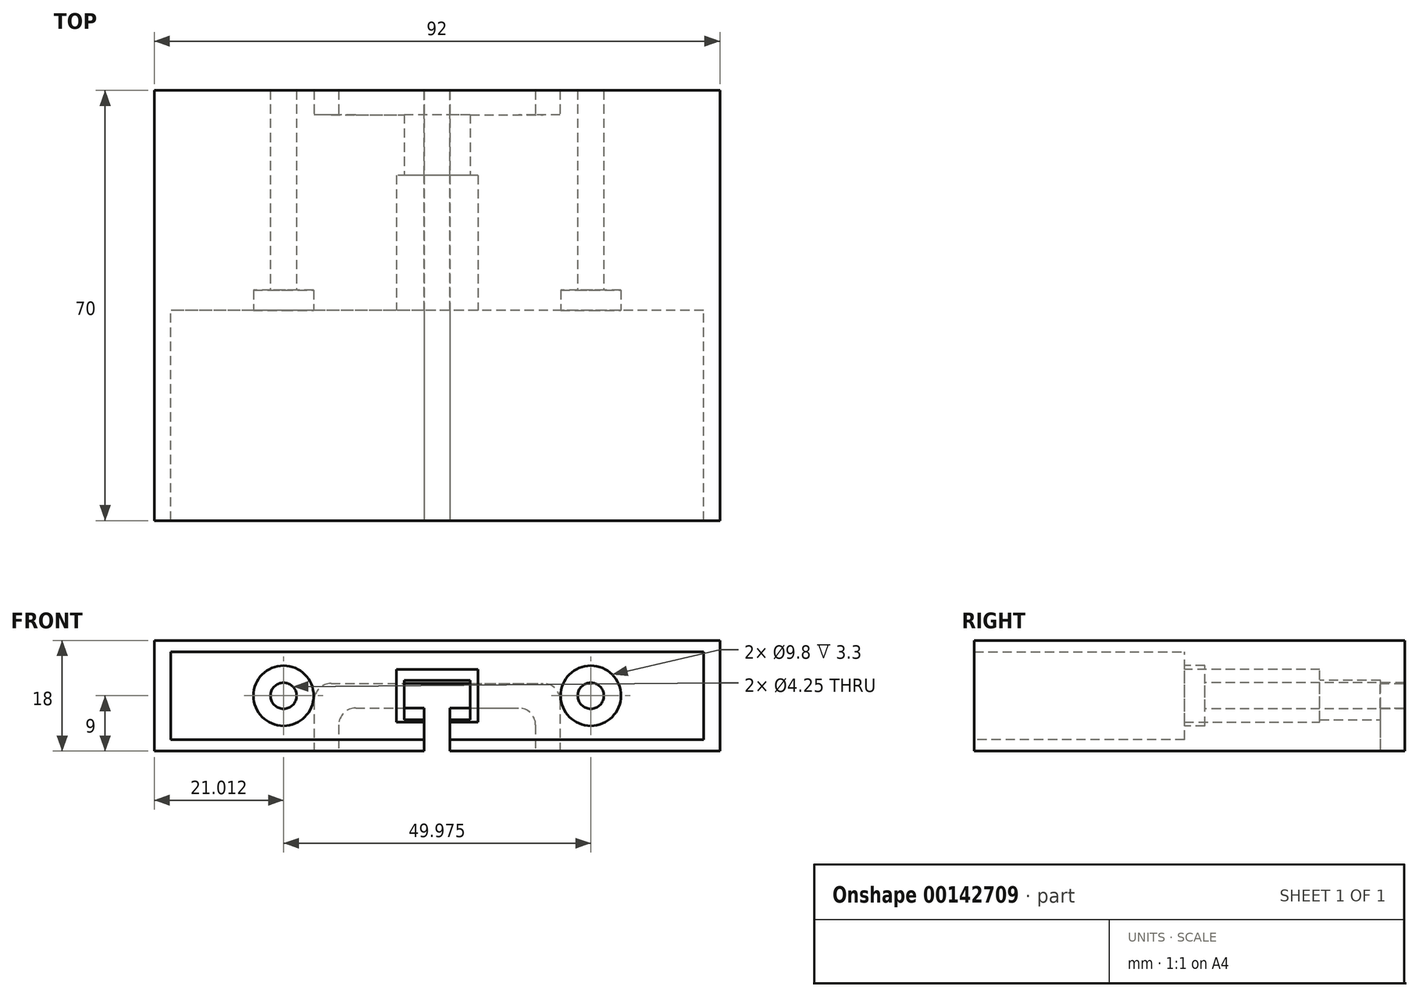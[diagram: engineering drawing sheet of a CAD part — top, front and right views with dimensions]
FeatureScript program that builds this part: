
annotation { "Feature Type Name" : "Feature", "Feature Type Description" : "" }
export const myFeature = defineFeature(function(context is Context, id is Id, definition is map)
    precondition{}
    {
        {
            var Q0;
            Q0=qCreatedBy(makeId("Front.planeOp"),FACE);
            var sketch = newSketch(context, id + "F0", { "sketchPlane" : qUnion([Q0])});
            skLineSegment(sketch, "E0.bottom", {"start": v(46, -9) * mm, "end": v(-46, -9) * mm});
            skLineSegment(sketch, "E0.top", {"start": v(46, 9) * mm, "end": v(-46, 9) * mm});
            skLineSegment(sketch, "E0.left", {"start": v(46, -9) * mm, "end": v(46, 9) * mm});
            skLineSegment(sketch, "E0.right", {"start": v(-46, -9) * mm, "end": v(-46, 9) * mm});
            skPoint(sketch, "E0.middle", {"position": v(0, 0) * mm});
            skLineSegment(sketch, "E1.bottom", {"start": v(43.33, -7.12) * mm, "end": v(-43.33, -7.13) * mm});
            skLineSegment(sketch, "E1.top", {"start": v(43.33, 7.13) * mm, "end": v(-43.33, 7.12) * mm});
            skLineSegment(sketch, "E1.left", {"start": v(43.33, -7.12) * mm, "end": v(43.33, 7.13) * mm});
            skLineSegment(sketch, "E1.right", {"start": v(-43.33, -7.13) * mm, "end": v(-43.33, 7.12) * mm});
            skSolve(sketch);
        }
        {
            var Q0;
            Q0=makeQuery(id+"F0.imprint","IMPRINT",FACE,{"disambiguationData":[TD([[makeQuery(id+"F0.imprint","IMPRINT",EDGE,{"derivedFrom":sQuery(id+"F0.wireOp",EDGE,"E0.bottom")}),-1.0]])]});
            extrude(context, id + "F1", {"entities" : qUnion([Q0]), "depth" : 70 * mm, "offsetDistance" : 25 * mm});
        }
        {
            var Q0;
            Q0=makeQuery(id+"F0.imprint","IMPRINT",FACE,{"disambiguationData":[TD([[makeQuery(id+"F0.imprint","IMPRINT",EDGE,{"derivedFrom":sQuery(id+"F0.wireOp",EDGE,"E1.bottom")}),-1.0]])]});
            extrude(context, id + "F2", {"entities" : qUnion([Q0]), "operationType" : NewBodyOperationType.ADD, "depth" : 35.8 * mm, "offsetDistance" : 25 * mm});
        }
        {
            var Q0;
            Q0=qCreatedBy(makeId("Front.planeOp"),FACE);
            var sketch = newSketch(context, id + "F3", { "sketchPlane" : qUnion([Q0])});
            skPoint(sketch, "E2.middle", {"position": v(0, 0) * mm});
            skCircle(sketch, "E3", {"center": v(0, 0) * mm, "radius": 2 * mm});
            skSolve(sketch);
        }
        {
            var Q0;
            Q0=makeQuery(id+"F2.opExtrude","CAP_FACE",FACE,{"disambiguationData":[OSD([sQuery(id+"F0.wireOp",EDGE,"E1.bottom"),sQuery(id+"F0.wireOp",EDGE,"E1.top"),sQuery(id+"F0.wireOp",EDGE,"E1.left"),sQuery(id+"F0.wireOp",EDGE,"E1.right")])],"isStart":false});
            var sketch = newSketch(context, id + "F4", { "sketchPlane" : qUnion([Q0])});
            skLineSegment(sketch, "E4.bottom", {"start": v(6.65, -4.3) * mm, "end": v(-6.65, -4.3) * mm});
            skLineSegment(sketch, "E4.top", {"start": v(6.65, 4.3) * mm, "end": v(-6.65, 4.3) * mm});
            skLineSegment(sketch, "E4.left", {"start": v(6.65, -4.3) * mm, "end": v(6.65, 4.3) * mm});
            skLineSegment(sketch, "E4.right", {"start": v(-6.65, -4.3) * mm, "end": v(-6.65, 4.3) * mm});
            skPoint(sketch, "E4.middle", {"position": v(0, 0) * mm});
            skSolve(sketch);
        }
        {
            var Q0;
            Q0=makeQuery(id+"F4.imprint","IMPRINT",FACE,{"disambiguationData":[TD([[makeQuery(id+"F4.imprint","IMPRINT",EDGE,{"derivedFrom":sQuery(id+"F4.wireOp",EDGE,"E4.bottom")}),-1.0]])]});
            extrude(context, id + "F5", {"entities" : qUnion([Q0]), "operationType" : NewBodyOperationType.REMOVE, "oppositeDirection" : true, "depth" : 22 * mm, "offsetDistance" : 25 * mm});
        }
        {
            var Q0;
            Q0 = qSketchRegion(id + "F3", true);
            extrude(context, id + "F6", {"entities" : qUnion([Q0]), "operationType" : NewBodyOperationType.REMOVE, "depth" : 8 * mm, "offsetDistance" : 25 * mm});
        }
        {
            var Q0;
            Q0=qCreatedBy(makeId("Front.planeOp"),FACE);
            var sketch = newSketch(context, id + "F7", { "sketchPlane" : qUnion([Q0])});
            skLineSegment(sketch, "E5.bottom", {"start": v(-13.25, -2) * mm, "end": v(13.25, -2) * mm});
            skLineSegment(sketch, "E5.top", {"start": v(-17.25, 2) * mm, "end": v(17.25, 2) * mm});
            skLineSegment(sketch, "E5.left", {"start": v(-20, -2) * mm, "end": v(-20, -0.75) * mm});
            skLineSegment(sketch, "E5.right", {"start": v(20, -2) * mm, "end": v(20, -0.75) * mm});
            skPoint(sketch, "E5.middle", {"position": v(0, 0) * mm});
            skLineSegment(sketch, "E6.bottom", {"start": v(17.25, 2) * mm, "end": v(16, 2) * mm});
            skLineSegment(sketch, "E6.top", {"start": v(20, -9.8) * mm, "end": v(16, -9.8) * mm});
            skLineSegment(sketch, "E6.left", {"start": v(20, -0.75) * mm, "end": v(20, -9.8) * mm});
            skLineSegment(sketch, "E6.right", {"start": v(16, -4.75) * mm, "end": v(16, -9.8) * mm});
            skLineSegment(sketch, "E7.bottom", {"start": v(-17.25, 2) * mm, "end": v(-16, 2) * mm});
            skLineSegment(sketch, "E7.top", {"start": v(-20, -11.9) * mm, "end": v(-16, -11.9) * mm});
            skLineSegment(sketch, "E7.left", {"start": v(-20, -0.75) * mm, "end": v(-20, -11.9) * mm});
            skLineSegment(sketch, "E7.right", {"start": v(-16, -4.75) * mm, "end": v(-16, -11.9) * mm});
            skPoint(sketch, "E8.visualSharp", {"position": v(-16, -2) * mm});
            skArc(sketch, "E8.filletArc", {"start": v(-13.25, -2) * mm, "mid": v(-15.2, -2.8) * mm, "end": v(-16, -4.75) * mm});
            skPoint(sketch, "E9.visualSharp", {"position": v(16, -2) * mm});
            skArc(sketch, "E9.filletArc", {"start": v(16, -4.75) * mm, "mid": v(15.2, -2.8) * mm, "end": v(13.25, -2) * mm});
            skPoint(sketch, "E10.visualSharp", {"position": v(-20, 2) * mm});
            skArc(sketch, "E10.filletArc", {"start": v(-17.25, 2) * mm, "mid": v(-19.2, 1.2) * mm, "end": v(-20, -0.75) * mm});
            skPoint(sketch, "E11.visualSharp", {"position": v(20, 2) * mm});
            skArc(sketch, "E11.filletArc", {"start": v(20, -0.75) * mm, "mid": v(19.2, 1.2) * mm, "end": v(17.25, 2) * mm});
            skSolve(sketch);
        }
        {
            var Q0;
            Q0 = qSketchRegion(id + "F7", true);
            extrude(context, id + "F8", {"entities" : qUnion([Q0]), "operationType" : NewBodyOperationType.REMOVE, "depth" : 4 * mm, "offsetDistance" : 25 * mm});
        }
        {
            var Q0;
            Q0=makeQuery(id+"F5.boolean.opBoolean","COPY",FACE,{"derivedFrom":makeQuery(id+"F5.opExtrude","CAP_FACE",FACE,{"disambiguationData":[OSD([sQuery(id+"F4.wireOp",EDGE,"E4.bottom"),sQuery(id+"F4.wireOp",EDGE,"E4.top"),sQuery(id+"F4.wireOp",EDGE,"E4.left"),sQuery(id+"F4.wireOp",EDGE,"E4.right")])],"isStart":false})});
            var sketch = newSketch(context, id + "F9", { "sketchPlane" : qUnion([Q0])});
            skCircle(sketch, "E12", {"center": v(0, -0.7) * mm, "radius": 3.2 * mm});
            skLineSegment(sketch, "E13.bottom", {"start": v(5.4, -3.92) * mm, "end": v(-5.4, -3.92) * mm});
            skLineSegment(sketch, "E13.top", {"start": v(5.4, 2.53) * mm, "end": v(-5.4, 2.53) * mm});
            skLineSegment(sketch, "E13.left", {"start": v(5.4, -3.92) * mm, "end": v(5.4, 2.53) * mm});
            skLineSegment(sketch, "E13.right", {"start": v(-5.4, -3.92) * mm, "end": v(-5.4, 2.53) * mm});
            skSolve(sketch);
        }
        {
            var Q0;
            Q0=makeQuery(id+"F9.imprint","IMPRINT",FACE,{"disambiguationData":[TD([[makeQuery(id+"F9.imprint","IMPRINT",EDGE,{"derivedFrom":sQuery(id+"F9.wireOp",EDGE,"E12")}),1.0]])]});
            var Q1;
            Q1=makeQuery(id+"F9.imprint","IMPRINT",FACE,{"disambiguationData":[TD([[makeQuery(id+"F9.imprint","IMPRINT",EDGE,{"derivedFrom":sQuery(id+"F9.wireOp",EDGE,"E12")}),-1.0]])]});
            extrude(context, id + "F10", {"entities" : qUnion([Q0, Q1]), "operationType" : NewBodyOperationType.REMOVE, "oppositeDirection" : true, "depth" : 9.9 * mm, "offsetDistance" : 25 * mm});
        }
        {
            var Q0;
            Q0=makeQuery(id+"F1.opExtrude","SWEPT_FACE",FACE,{"disambiguationData":[OSD([sQuery(id+"F0.wireOp",EDGE,"E0.bottom")])]});
            var sketch = newSketch(context, id + "F11", { "sketchPlane" : qUnion([Q0])});
            skPoint(sketch, "E14", {"position": v(0, 1.31) * mm});
            skLineSegment(sketch, "E15.bottom", {"start": v(2.1, -78.69) * mm, "end": v(-2.1, -78.69) * mm});
            skLineSegment(sketch, "E15.top", {"start": v(2.1, 81.31) * mm, "end": v(-2.1, 81.31) * mm});
            skLineSegment(sketch, "E15.left", {"start": v(2.1, -78.69) * mm, "end": v(2.1, 81.31) * mm});
            skLineSegment(sketch, "E15.right", {"start": v(-2.1, -78.69) * mm, "end": v(-2.1, 81.31) * mm});
            skSolve(sketch);
        }
        {
            var Q0;
            {var subQ0=sQuery(id+"F11.wireOp",EDGE,"E15.left");var subQ5=sQuery(id+"F0.wireOp",EDGE,"E0.bottom");var subQ8=makeQuery(id+"F1.opExtrude","CAP_EDGE",EDGE,{"disambiguationData":[OSD([subQ5])],"isStart":false});var subQ9=makeQuery(id+"F11.imprint","INTERSECT",VERTEX,{"derivedFrom":[subQ8,subQ0]});Q0=makeQuery(id+"F11.imprint","IMPRINT",FACE,{"disambiguationData":[TD([[makeQuery(id+"F11.imprint","IMPRINT",EDGE,{"disambiguationData":[TD([[subQ9,-1.0]])],"derivedFrom":subQ8}),1.0]])]});}
            extrude(context, id + "F12", {"entities" : qUnion([Q0]), "operationType" : NewBodyOperationType.REMOVE, "oppositeDirection" : true, "depth" : 8.9 * mm, "offsetDistance" : 25 * mm});
        }
        {
            var Q0;
            Q0=makeQuery(id+"F2.opExtrude","CAP_FACE",FACE,{"disambiguationData":[OSD([sQuery(id+"F0.wireOp",EDGE,"E1.bottom"),sQuery(id+"F0.wireOp",EDGE,"E1.top"),sQuery(id+"F0.wireOp",EDGE,"E1.left"),sQuery(id+"F0.wireOp",EDGE,"E1.right")])],"isStart":false});
            var sketch = newSketch(context, id + "F13", { "sketchPlane" : qUnion([Q0])});
            skPoint(sketch, "E16", {"position": v(-24.99, 0) * mm});
            skPoint(sketch, "E17", {"position": v(24.99, 0) * mm});
            skCircle(sketch, "E18", {"center": v(-24.99, 0) * mm, "radius": 4.9 * mm});
            skCircle(sketch, "E19", {"center": v(24.99, 0) * mm, "radius": 4.9 * mm});
            skCircle(sketch, "E20", {"center": v(-24.99, 0) * mm, "radius": 2.12 * mm});
            skCircle(sketch, "E21", {"center": v(24.99, 0) * mm, "radius": 2.12 * mm});
            skPoint(sketch, "E22.orphan", {"position": v(-43.33, 0) * mm});
            skPoint(sketch, "E23.end.orphan", {"position": v(-6.65, 0) * mm});
            skPoint(sketch, "E24.orphan", {"position": v(6.65, 0) * mm});
            skPoint(sketch, "E25.end.orphan", {"position": v(43.33, 0) * mm});
            skSolve(sketch);
        }
        {
            var Q0;
            Q0=makeQuery(id+"F13.imprint","IMPRINT",FACE,{"disambiguationData":[TD([[makeQuery(id+"F13.imprint","IMPRINT",EDGE,{"derivedFrom":sQuery(id+"F13.wireOp",EDGE,"E19")}),1.0]])]});
            var Q1;
            Q1=makeQuery(id+"F13.imprint","IMPRINT",FACE,{"disambiguationData":[TD([[makeQuery(id+"F13.imprint","IMPRINT",EDGE,{"derivedFrom":sQuery(id+"F13.wireOp",EDGE,"E18")}),1.0]])]});
            var Q2;
            Q2=makeQuery(id+"F13.imprint","IMPRINT",FACE,{"disambiguationData":[TD([[makeQuery(id+"F13.imprint","IMPRINT",EDGE,{"derivedFrom":sQuery(id+"F13.wireOp",EDGE,"E20")}),1.0]])]});
            var Q3;
            Q3=makeQuery(id+"F13.imprint","IMPRINT",FACE,{"disambiguationData":[TD([[makeQuery(id+"F13.imprint","IMPRINT",EDGE,{"derivedFrom":sQuery(id+"F13.wireOp",EDGE,"E21")}),1.0]])]});
            extrude(context, id + "F14", {"entities" : qUnion([Q0, Q1, Q2, Q3]), "operationType" : NewBodyOperationType.REMOVE, "oppositeDirection" : true, "depth" : 3.3 * mm, "offsetDistance" : 25 * mm});
        }
        {
            var Q0;
            Q0=makeQuery(id+"F13.imprint","IMPRINT",FACE,{"disambiguationData":[TD([[makeQuery(id+"F13.imprint","IMPRINT",EDGE,{"derivedFrom":sQuery(id+"F13.wireOp",EDGE,"E20")}),1.0]])]});
            var Q1;
            Q1=makeQuery(id+"F13.imprint","IMPRINT",FACE,{"disambiguationData":[TD([[makeQuery(id+"F13.imprint","IMPRINT",EDGE,{"derivedFrom":sQuery(id+"F13.wireOp",EDGE,"E21")}),1.0]])]});
            extrude(context, id + "F15", {"entities" : qUnion([Q0, Q1]), "operationType" : NewBodyOperationType.REMOVE, "oppositeDirection" : true, "depth" : 44.7 * mm, "offsetDistance" : 25 * mm});
        }
    });
